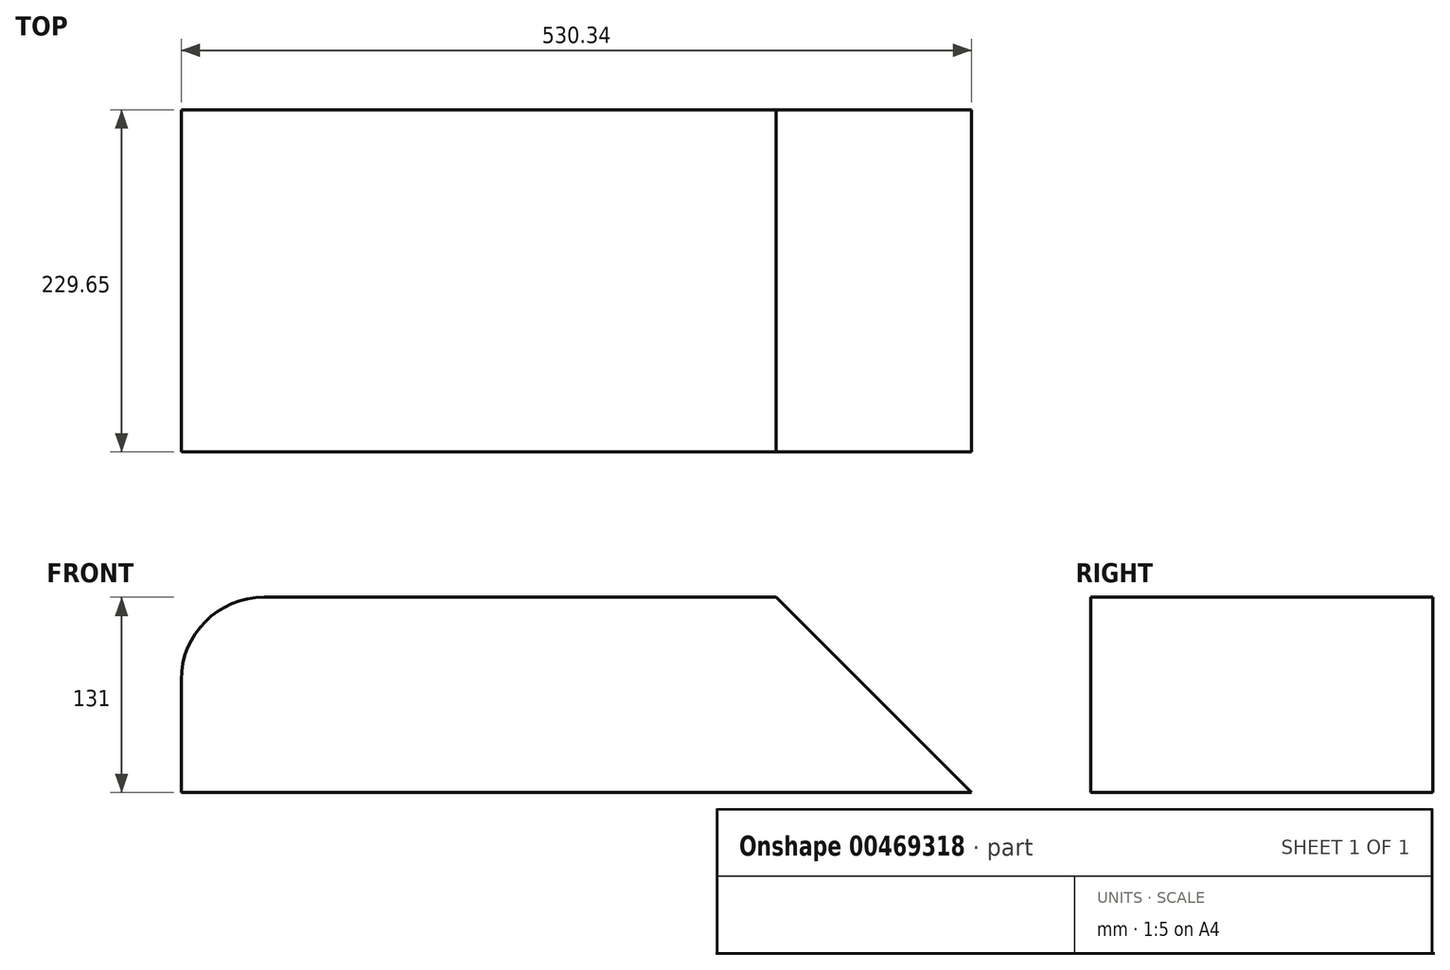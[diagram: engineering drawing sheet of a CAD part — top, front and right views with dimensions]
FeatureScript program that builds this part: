
annotation { "Feature Type Name" : "Feature", "Feature Type Description" : "" }
export const myFeature = defineFeature(function(context is Context, id is Id, definition is map)
    precondition{}
    {
        {
            var Q0;
            Q0=qCreatedBy(makeId("Top.planeOp"),FACE);
            var sketch = newSketch(context, id + "F0", { "sketchPlane" : qUnion([Q0])});
            skLineSegment(sketch, "E0.bottom", {"start": v(-330.58, 57.82) * mm, "end": v(268.76, 57.82) * mm});
            skLineSegment(sketch, "E0.top", {"start": v(-330.58, -171.83) * mm, "end": v(268.76, -171.83) * mm});
            skLineSegment(sketch, "E0.left", {"start": v(-330.58, 57.82) * mm, "end": v(-330.58, -171.83) * mm});
            skLineSegment(sketch, "E0.right", {"start": v(268.76, 57.82) * mm, "end": v(268.76, -171.83) * mm});
            skSolve(sketch);
        }
        {
            var Q0;
            Q0=makeQuery(id+"F0.imprint","IMPRINT",FACE,{"disambiguationData":[TD([[makeQuery(id+"F0.imprint","IMPRINT",EDGE,{"derivedFrom":sQuery(id+"F0.wireOp",EDGE,"E0.bottom")}),-1.0]])]});
            extrude(context, id + "F1", {"entities" : qUnion([Q0]), "depth" : 131 * mm});
        }
        {
            var Q0;
            Q0=makeQuery(id+"F1.opExtrude","CAP_EDGE",EDGE,{"disambiguationData":[OSD([sQuery(id+"F0.wireOp",EDGE,"E0.left")])],"isStart":false});
            fillet(context, id + "F2", {"entities" : qUnion([Q0]), "radius" : 55.53 * mm, "tangentPropagation" : true, "allowEdgeOverflow" : false});
        }
        {
            var Q0;
            Q0=makeQuery(id+"F1.opExtrude","CAP_EDGE",EDGE,{"disambiguationData":[OSD([sQuery(id+"F0.wireOp",EDGE,"E0.right")])],"isStart":false});
            chamfer(context, id + "F3", {"entities" : qUnion([Q0]), "width" : 200 * mm, "tangentPropagation" : true});
        }
    });
